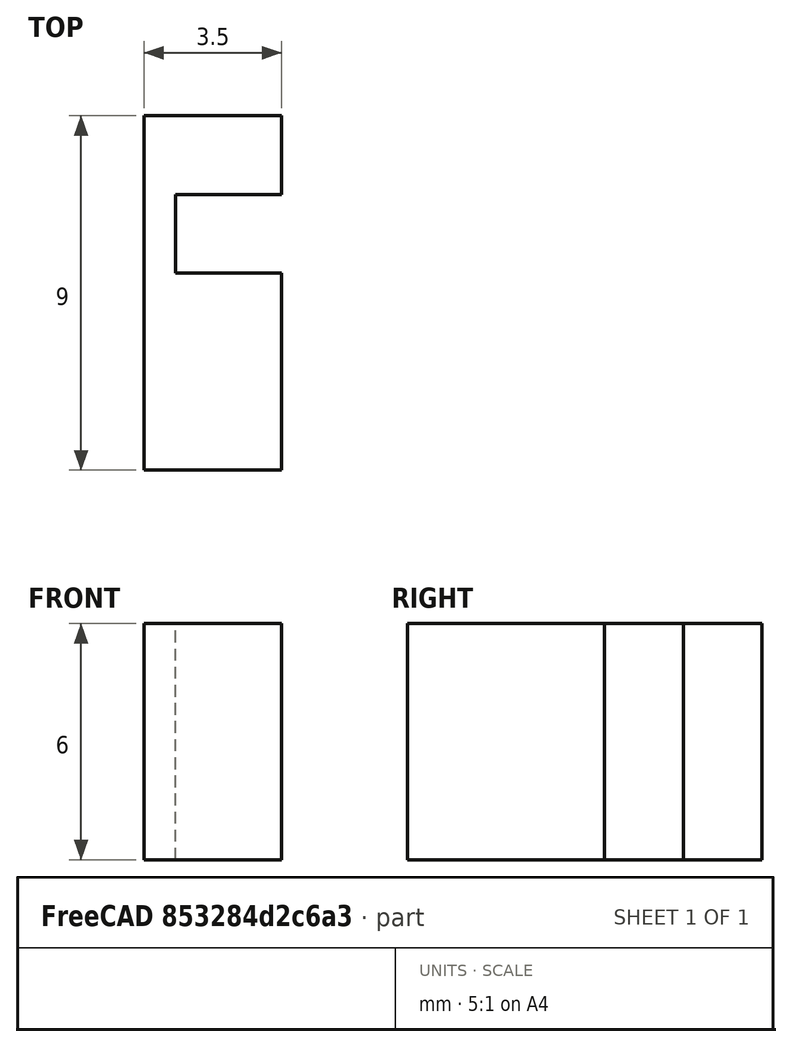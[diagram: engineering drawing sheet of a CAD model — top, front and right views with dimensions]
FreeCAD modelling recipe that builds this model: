
FCSTD DOCUMENT  (FreeCAD 0.21R33771 (Git))
Label: 6IN8SHELL-PAD08
License: All rights reserved
LicenseURL: http://en.wikipedia.org/wiki/All_rights_reserved
objects: Sketcher::SketchObject×1, PartDesign::Pad×1, PartDesign::Body×1
note: 4 computed .brp shape members not serialized (recipe doc carries the construction recipe); baked Part::Feature solids carry a one-line shape summary decoded from their .brp

FEATURE [Sketcher::SketchObject] Sketch
  FullyConstrained = true
  MapMode = 5
  Support = -> [XY_Plane]
  sketch-geometry (8):
    g0: LineSegment StartX=0 StartY=0 StartZ=0 EndX=0 EndY=9 EndZ=0
    g1: LineSegment StartX=0 StartY=9 StartZ=0 EndX=3.5 EndY=9 EndZ=0
    g2: LineSegment StartX=3.5 StartY=9 StartZ=0 EndX=3.5 EndY=7 EndZ=0
    g3: LineSegment StartX=3.5 StartY=7 StartZ=0 EndX=0.8 EndY=7 EndZ=0
    g4: LineSegment StartX=0.8 StartY=7 StartZ=0 EndX=0.8 EndY=5 EndZ=0
    g5: LineSegment StartX=0.8 StartY=5 StartZ=0 EndX=3.5 EndY=5 EndZ=0
    g6: LineSegment StartX=3.5 StartY=0 StartZ=0 EndX=0 EndY=0 EndZ=0
    g7: LineSegment StartX=3.5 StartY=5 StartZ=0 EndX=3.5 EndY=0 EndZ=0
  constraints (24):
    c: Coincident(g0,g-1)
    c: PointOnObject(g0,g-2)
    c: Horizontal(g1)
    c: Coincident(g2,g1)
    c: Vertical(g2)
    c: Horizontal(g3)
    c: Vertical(g4)
    c: Coincident(g5,g4)
    c: Horizontal(g5)
    c: PointOnObject(g6,g-1)
    c: PointOnObject(g6,g-2)
    c: Horizontal(g6)
    c: Coincident(g2,g3)
    c: Coincident(g3,g4)
    c: DistanceY(g4,g4) = 2
    c: Coincident(g0,g1)
    c: DistanceY(g2,g2) = 2
    c: DistanceX(g1,g1) = 3.5
    c: DistanceX(g6,g6) = 3.5
    c: DistanceX(g0,g4) = 0.8
    c: Coincident(g7,g5)
    c: Coincident(g7,g6)
    c: Vertical(g7)
    c: DistanceY(g7,g7) = 5
FEATURE [PartDesign::Pad] Pad
  Direction = (0,0,1)
  Length = 6
  Length2 = 10
  Profile = -> Sketch
  ReferenceAxis = -> Sketch [N_Axis]
  Type = 0
FEATURE [PartDesign::Body] Body
  Group = -> [Sketch,Pad]
  Origin = -> Origin
  Tip = -> Pad
